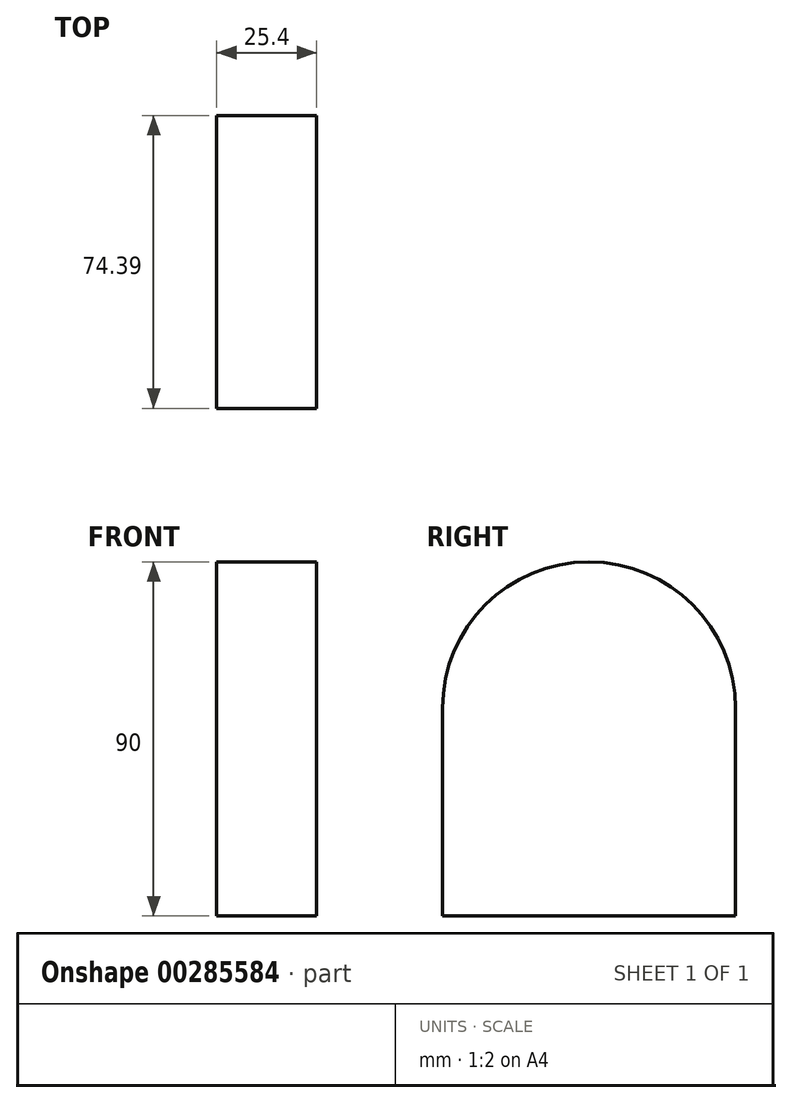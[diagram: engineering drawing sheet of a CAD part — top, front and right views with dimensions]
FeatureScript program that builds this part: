
annotation { "Feature Type Name" : "Feature", "Feature Type Description" : "" }
export const myFeature = defineFeature(function(context is Context, id is Id, definition is map)
    precondition{}
    {
        {
            var Q0;
            Q0=qCreatedBy(makeId("Right.planeOp"),FACE);
            var sketch = newSketch(context, id + "F0", { "sketchPlane" : qUnion([Q0])});
            skLineSegment(sketch, "E0.bottom", {"start": v(-193.6, 29.55) * mm, "end": v(-119.2, 29.55) * mm});
            skLineSegment(sketch, "E0.top", {"start": v(-193.6, -2.33) * mm, "end": v(-119.2, -2.33) * mm});
            skLineSegment(sketch, "E0.left", {"start": v(-193.6, 29.55) * mm, "end": v(-193.6, -2.33) * mm});
            skLineSegment(sketch, "E0.right", {"start": v(-119.2, 29.55) * mm, "end": v(-119.2, -2.33) * mm});
            skArc(sketch, "E1", {"start": v(-119.2, 29.55) * mm, "mid": v(-156.4, 66.74) * mm, "end": v(-193.6, 29.55) * mm});
            skLineSegment(sketch, "E2", {"start": v(-193.6, -2.33) * mm, "end": v(-193.6, -23.26) * mm});
            skLineSegment(sketch, "E3", {"start": v(-119.2, -2.33) * mm, "end": v(-119.2, -23.26) * mm});
            skLineSegment(sketch, "E4", {"start": v(-119.2, -23.26) * mm, "end": v(-193.6, -23.26) * mm});
            skSolve(sketch);
        }
        {
            var Q0;
            Q0=makeQuery(id+"F0.imprint","IMPRINT",FACE,{"disambiguationData":[TD([[makeQuery(id+"F0.imprint","IMPRINT",EDGE,{"derivedFrom":sQuery(id+"F0.wireOp",EDGE,"E0.bottom")}),1.0]])]});
            var Q1;
            Q1=makeQuery(id+"F0.imprint","IMPRINT",FACE,{"disambiguationData":[TD([[makeQuery(id+"F0.imprint","IMPRINT",EDGE,{"derivedFrom":sQuery(id+"F0.wireOp",EDGE,"E0.bottom")}),-1.0]])]});
            var Q2;
            Q2=makeQuery(id+"F0.imprint","IMPRINT",FACE,{"disambiguationData":[TD([[makeQuery(id+"F0.imprint","IMPRINT",EDGE,{"derivedFrom":sQuery(id+"F0.wireOp",EDGE,"E0.top")}),-1.0]])]});
            extrude(context, id + "F1", {"entities" : qUnion([Q0, Q1, Q2]), "depth" : 25.4 * mm});
        }
    });
